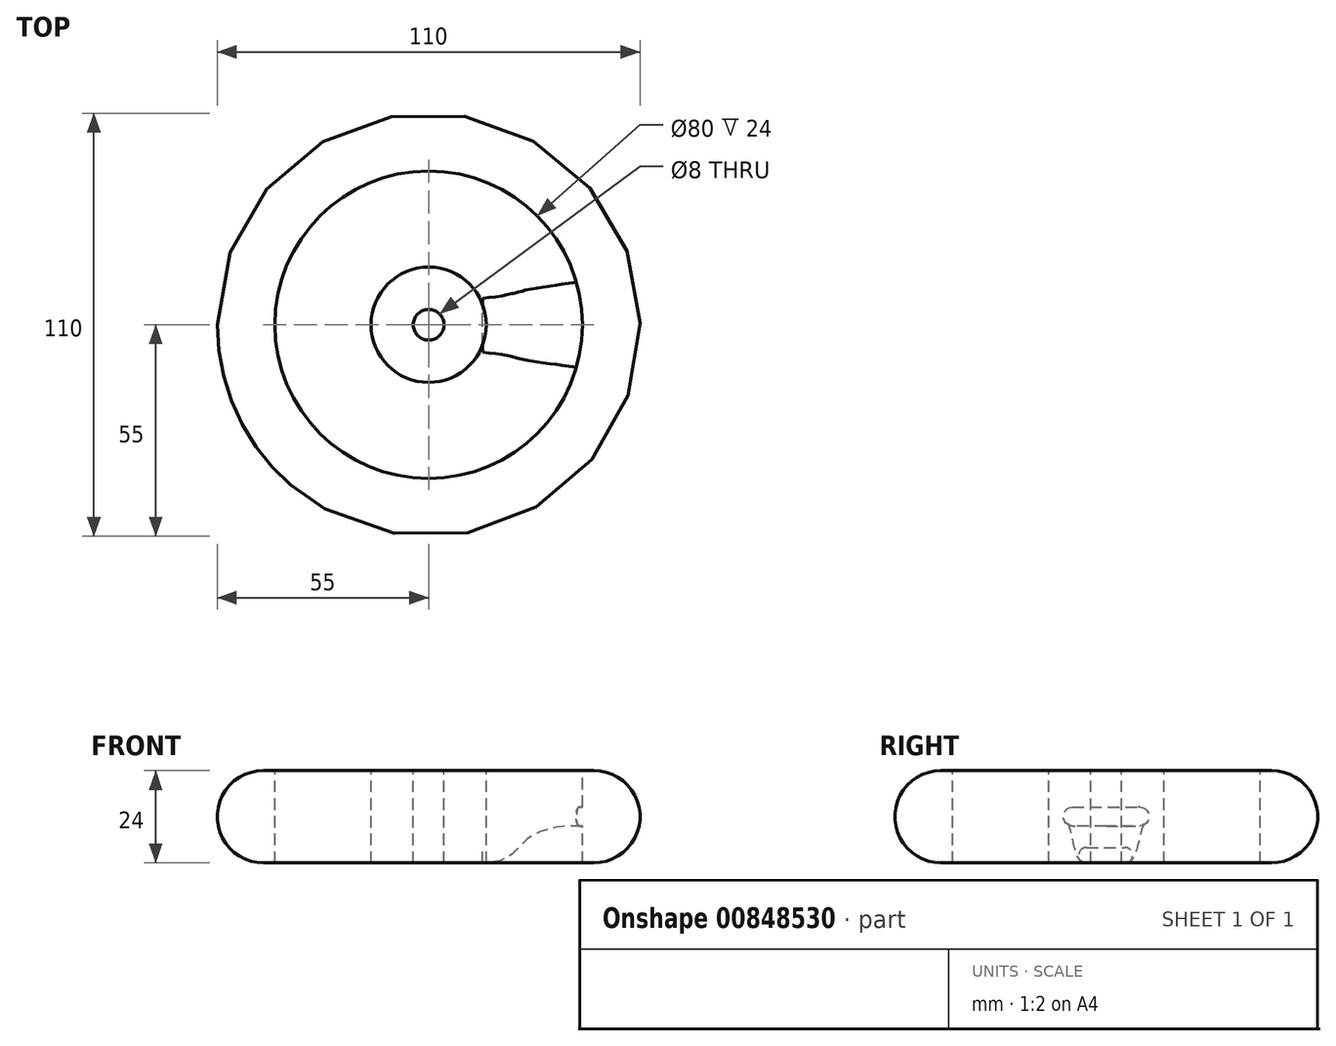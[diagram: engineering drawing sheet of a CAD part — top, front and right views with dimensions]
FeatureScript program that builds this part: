
annotation { "Feature Type Name" : "Feature", "Feature Type Description" : "" }
export const myFeature = defineFeature(function(context is Context, id is Id, definition is map)
    precondition{}
    {
        {
            var Q0;
            Q0=qCreatedBy(makeId("Top.planeOp"),FACE);
            var sketch = newSketch(context, id + "F0", { "sketchPlane" : qUnion([Q0])});
            skCircle(sketch, "E0", {"center": v(0, 0) * mm, "radius": 40 * mm});
            skSolve(sketch);
        }
        {
            var Q0;
            Q0=qCreatedBy(makeId("Front.planeOp"),FACE);
            var sketch = newSketch(context, id + "F1", { "sketchPlane" : qUnion([Q0])});
            skArc(sketch, "E1", {"start": v(-43, 12) * mm, "mid": v(-55, 0) * mm, "end": v(-43, -12) * mm});
            skLineSegment(sketch, "E2", {"start": v(-43, 12) * mm, "end": v(-40, 12) * mm});
            skLineSegment(sketch, "E3", {"start": v(-43, -12) * mm, "end": v(-40, -12) * mm});
            skLineSegment(sketch, "E4", {"start": v(-40, -12) * mm, "end": v(-40, 12) * mm});
            skSolve(sketch);
        }
        {
            var Q0;
            Q0 = qSketchRegion(id + "F1", true);
            var Q1;
            Q1 = qConstructionFilter(qBodyType(qCreatedBy(id + "F0" ,EDGE), BodyType.WIRE), ConstructionObject.NO);
            sweep(context, id + "F2", {"profiles" : qUnion([Q0]), "path" : qUnion([Q1])});
        }
        {
            var Q0;
            Q0=qCreatedBy(makeId("Right.planeOp"),FACE);
            cPlane(context, id + "F3", {"entities" : qUnion([Q0]), "cplaneType" : CPlaneType.OFFSET, "offset" : 40 * mm, "width" : 150 * mm, "height" : 150 * mm});
        }
        {
            var Q0;
            Q0=qCreatedBy(id+"F3.planeOp",FACE);
            var sketch = newSketch(context, id + "F4", { "sketchPlane" : qUnion([Q0])});
            skLineSegment(sketch, "E5", {"start": v(-9, 0) * mm, "end": v(9, 0) * mm});
            skArc(sketch, "E6.0.startCap", {"start": v(-9, -2.5) * mm, "mid": v(-11.5, 0) * mm, "end": v(-9, 2.5) * mm});
            skArc(sketch, "E6.0.endCap", {"start": v(9, 2.5) * mm, "mid": v(11.5, 0) * mm, "end": v(9, -2.5) * mm});
            skLineSegment(sketch, "E6.0.left", {"start": v(-9, 2.5) * mm, "end": v(9, 2.5) * mm});
            skLineSegment(sketch, "E6.0.right", {"start": v(-9, -2.5) * mm, "end": v(9, -2.5) * mm});
            skPoint(sketch, "E7", {"position": v(0, 0) * mm});
            skSolve(sketch);
        }
        {
            var Q0;
            Q0=qCreatedBy(makeId("Right.planeOp"),FACE);
            cPlane(context, id + "F5", {"entities" : qUnion([Q0]), "cplaneType" : CPlaneType.OFFSET, "offset" : 14 * mm, "width" : 150 * mm, "height" : 150 * mm});
        }
        {
            var Q0;
            Q0=qCreatedBy(id+"F5.planeOp",FACE);
            var sketch = newSketch(context, id + "F6", { "sketchPlane" : qUnion([Q0])});
            skLineSegment(sketch, "E8", {"start": v(-5, -10) * mm, "end": v(5, -10) * mm});
            skArc(sketch, "E9.0.startCap", {"start": v(-5.15, -12) * mm, "mid": v(-7.15, -10) * mm, "end": v(-5.15, -8) * mm});
            skArc(sketch, "E9.0.endCap", {"start": v(4.85, -8) * mm, "mid": v(6.85, -10) * mm, "end": v(4.85, -12) * mm});
            skLineSegment(sketch, "E9.0.left", {"start": v(-5.15, -8) * mm, "end": v(4.85, -8) * mm});
            skLineSegment(sketch, "E9.0.right", {"start": v(-5.15, -12) * mm, "end": v(4.85, -12) * mm});
            skPoint(sketch, "E10", {"position": v(0, 0) * mm});
            skPoint(sketch, "E11", {"position": v(0, -10) * mm});
            skSolve(sketch);
        }
        {
            var Q0;
            Q0=qCreatedBy(makeId("Front.planeOp"),FACE);
            var sketch = newSketch(context, id + "F7", { "sketchPlane" : qUnion([Q0])});
            skFitSpline(sketch, "E12", {"points": [v(14, -12) * mm, v(21.72, -9.66) * mm, v(26.28, -5.37) * mm, v(34.67, -2.54) * mm, v(40, -2.5) * mm], "startDerivative": vector(42.8, -0.7) * mm, "endDerivative": vector(12.78, -1.24) * mm});
            skSolve(sketch);
        }
        {
            var Q1;
            Q1 = qSketchRegion(id + "F4", true);
            var Q2;
            Q2 = qSketchRegion(id + "F6", true);
            var Q3;
            Q3 = qConstructionFilter(qBodyType(qCreatedBy(id + "F7" ,EDGE), BodyType.WIRE), ConstructionObject.NO);
            loft(context, id + "F8", {"operationType" : NewBodyOperationType.ADD, "addGuides" : true, "sheetProfilesArray" : [{ "sheetProfileEntities" : qUnion([Q1]) }, { "sheetProfileEntities" : qUnion([Q2]) }], "guidesArray" : [{ "guideEntities" : qUnion([Q3]), "guideDerivativeType" : LoftGuideDerivativeType.DEFAULT, "guideDerivativeMagnitude" : 1 }]});
        }
        {
            var Q0;
            Q0=qCreatedBy(makeId("Front.planeOp"),FACE);
            var sketch = newSketch(context, id + "F9", { "sketchPlane" : qUnion([Q0])});
            skPoint(sketch, "E13.middle", {"position": v(0, 0) * mm});
            skLineSegment(sketch, "E14.bottom", {"start": v(0, 12) * mm, "end": v(15, 12) * mm});
            skLineSegment(sketch, "E14.top", {"start": v(0, -12) * mm, "end": v(15, -12) * mm});
            skLineSegment(sketch, "E14.left", {"start": v(0, 12) * mm, "end": v(0, -12) * mm});
            skLineSegment(sketch, "E14.right", {"start": v(15, 12) * mm, "end": v(15, -12) * mm});
            skSolve(sketch);
        }
        {
            var Q0;
            Q0 = qSketchRegion(id + "F9", true);
            var Q1;
            Q1=sQuery(id+"F9.wireOp",EDGE,"E14.left");
            revolve(context, id + "F10", {"surfaceOperationType" : NewSurfaceOperationType.NEW, "entities" : qUnion([Q0]), "axis" : qUnion([Q1]), "revolveType" : RevolveType.FULL});
        }
        {
            var Q0;
            Q0=makeQuery(id+"F10.opRevolve","SWEPT_FACE",FACE,{"disambiguationData":[OSD([sQuery(id+"F9.wireOp",EDGE,"E14.bottom")])]});
            var sketch = newSketch(context, id + "F11", { "sketchPlane" : qUnion([Q0])});
            skPoint(sketch, "E15", {"position": v(0, 0) * mm});
            skSolve(sketch);
        }
        {
            var Q0;
            Q0=sQuery(id+"F11.wireOp",VERTEX,"E15");
            var Q1;
            Q1=makeQuery(id+"F10.opRevolve","SWEPT_BODY",BODY,{"disambiguationData":[OSD([sQuery(id+"F9.wireOp",EDGE,"E14.bottom"),sQuery(id+"F9.wireOp",EDGE,"E14.top"),sQuery(id+"F9.wireOp",EDGE,"E14.left"),sQuery(id+"F9.wireOp",EDGE,"E14.right")])]});
            hole(context, id + "F12", {"style" : HoleStyle.SIMPLE, "endStyle" : HoleEndStyle.THROUGH, "holeDiameter" : 8 * mm, "majorDiameter" : 5 * mm, "isTappedThrough" : true, "tappedDepth" : 12 * mm, "tapClearance" : 3, "locations" : qUnion([Q0]), "scope" : qUnion([Q1])});
        }
    });
